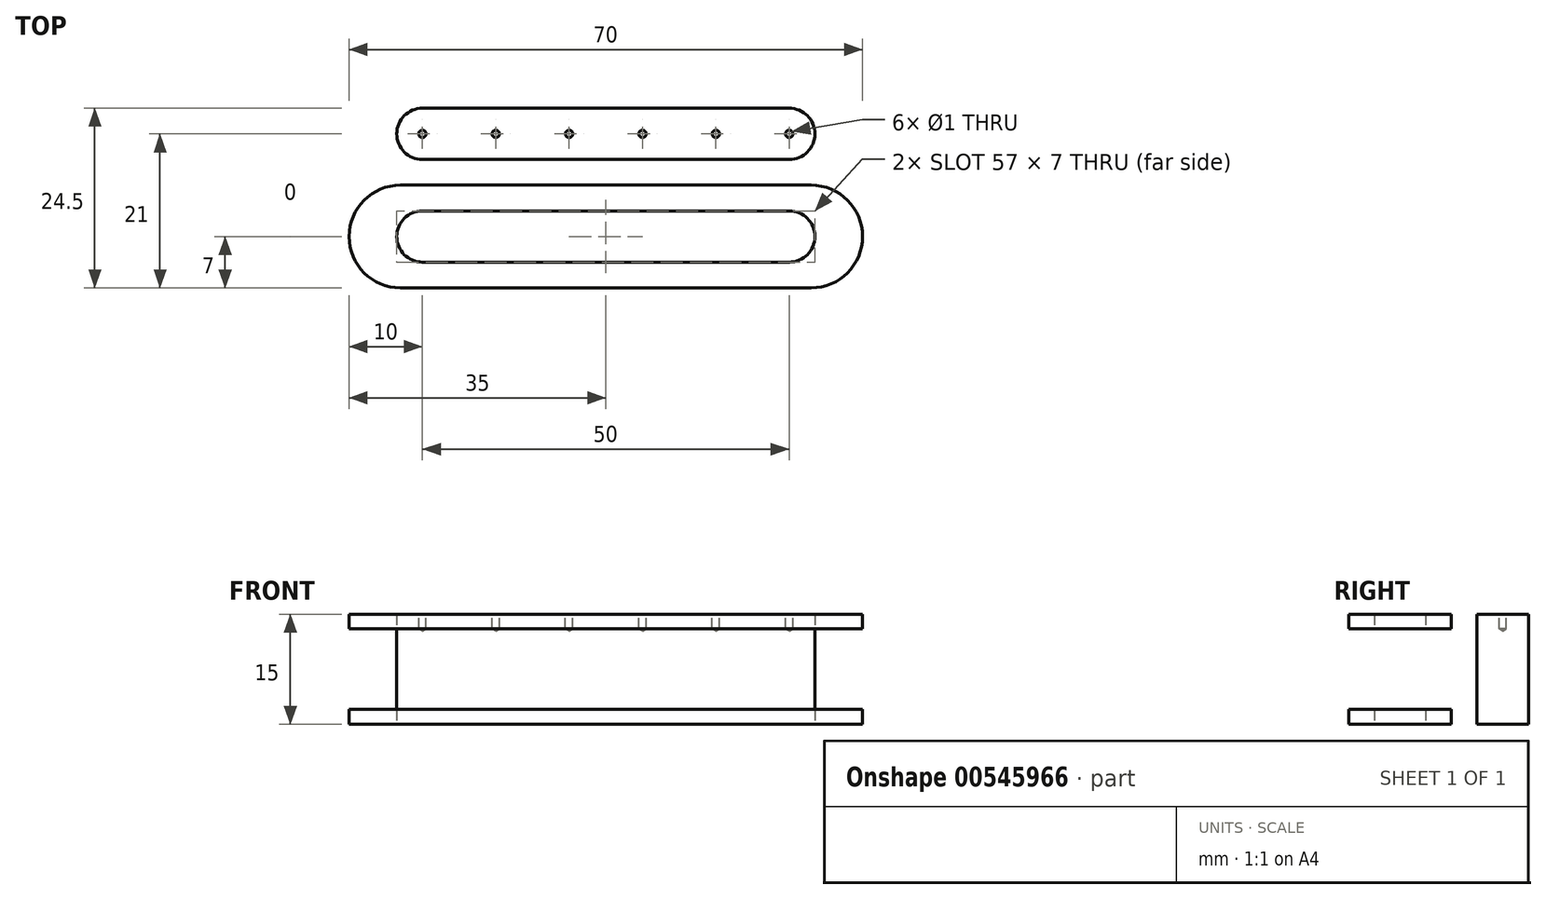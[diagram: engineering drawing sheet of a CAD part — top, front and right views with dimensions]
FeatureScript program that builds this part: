
annotation { "Feature Type Name" : "Feature", "Feature Type Description" : "" }
export const myFeature = defineFeature(function(context is Context, id is Id, definition is map)
    precondition{}
    {
        {
            var Q0;
            Q0=qCreatedBy(makeId("Top.planeOp"),FACE);
            var sketch = newSketch(context, id + "F0", { "sketchPlane" : qUnion([Q0])});
            skLineSegment(sketch, "E0.bottom", {"start": v(28, -7) * mm, "end": v(-28, -7) * mm});
            skLineSegment(sketch, "E0.top", {"start": v(28, 7) * mm, "end": v(-28, 7) * mm});
            skLineSegment(sketch, "E0.left", {"start": v(35, 0) * mm, "end": v(35, 0) * mm});
            skLineSegment(sketch, "E0.right", {"start": v(-35, 0) * mm, "end": v(-35, 0) * mm});
            skPoint(sketch, "E0.middle", {"position": v(0, 0) * mm});
            skPoint(sketch, "E1.visualSharp", {"position": v(-35, 7) * mm});
            skArc(sketch, "E1.filletArc", {"start": v(-28, 7) * mm, "mid": v(-32.95, 4.95) * mm, "end": v(-35, 0) * mm});
            skPoint(sketch, "E2.visualSharp", {"position": v(-35, -7) * mm});
            skArc(sketch, "E2.filletArc", {"start": v(-35, 0) * mm, "mid": v(-32.95, -4.95) * mm, "end": v(-28, -7) * mm});
            skPoint(sketch, "E3.visualSharp", {"position": v(35, 7) * mm});
            skArc(sketch, "E3.filletArc", {"start": v(35, 0) * mm, "mid": v(32.95, 4.95) * mm, "end": v(28, 7) * mm});
            skPoint(sketch, "E4.visualSharp", {"position": v(35, -7) * mm});
            skArc(sketch, "E4.filletArc", {"start": v(28, -7) * mm, "mid": v(32.95, -4.95) * mm, "end": v(35, 0) * mm});
            skPoint(sketch, "E5", {"position": v(15, 0) * mm});
            skPoint(sketch, "E6", {"position": v(5, 0) * mm});
            skPoint(sketch, "E7", {"position": v(-5, 0) * mm});
            skPoint(sketch, "E8", {"position": v(-15, 0) * mm});
            skPoint(sketch, "E9", {"position": v(-25, 0) * mm});
            skPoint(sketch, "E10", {"position": v(25, 0) * mm});
            skLineSegment(sketch, "E11.bottom", {"start": v(25, 3.5) * mm, "end": v(-25, 3.5) * mm});
            skLineSegment(sketch, "E11.top", {"start": v(25, -3.5) * mm, "end": v(-25, -3.5) * mm});
            skLineSegment(sketch, "E11.left", {"start": v(28.5, 0) * mm, "end": v(28.5, 0) * mm});
            skLineSegment(sketch, "E11.right", {"start": v(-28.5, 0) * mm, "end": v(-28.5, 0) * mm});
            skPoint(sketch, "E12.visualSharp", {"position": v(-28.5, 3.5) * mm});
            skArc(sketch, "E12.filletArc", {"start": v(-25, 3.5) * mm, "mid": v(-27.47, 2.47) * mm, "end": v(-28.5, 0) * mm});
            skPoint(sketch, "E13.visualSharp", {"position": v(-28.5, -3.5) * mm});
            skArc(sketch, "E13.filletArc", {"start": v(-28.5, 0) * mm, "mid": v(-27.47, -2.47) * mm, "end": v(-25, -3.5) * mm});
            skPoint(sketch, "E14.visualSharp", {"position": v(28.5, -3.5) * mm});
            skArc(sketch, "E14.filletArc", {"start": v(25, -3.5) * mm, "mid": v(27.47, -2.47) * mm, "end": v(28.5, 0) * mm});
            skPoint(sketch, "E15.visualSharp", {"position": v(28.5, 3.5) * mm});
            skArc(sketch, "E15.filletArc", {"start": v(28.5, 0) * mm, "mid": v(27.47, 2.47) * mm, "end": v(25, 3.5) * mm});
            skSolve(sketch);
        }
        {
            var Q0;
            Q0=makeQuery(id+"F0.imprint","IMPRINT",FACE,{"disambiguationData":[TD([[makeQuery(id+"F0.imprint","IMPRINT",EDGE,{"derivedFrom":sQuery(id+"F0.wireOp",EDGE,"E11.bottom")}),1.0]])]});
            extrude(context, id + "F1", {"entities" : qUnion([Q0]), "depth" : 15 * mm, "offsetDistance" : 25 * mm});
        }
        {
            var Q0;
            Q0=qSketchRegion(id+"F0",true);
            extrude(context, id + "F2", {"entities" : qUnion([Q0]), "depth" : 2 * mm, "offsetDistance" : 25 * mm});
        }
        {
            var Q0;
            Q0=makeQuery(id+"F2.opExtrude","SWEPT_BODY",BODY,{"disambiguationData":[OSD([sQuery(id+"F0.wireOp",EDGE,"E0.bottom"),sQuery(id+"F0.wireOp",EDGE,"E0.top"),sQuery(id+"F0.wireOp",EDGE,"E1.filletArc"),sQuery(id+"F0.wireOp",EDGE,"E2.filletArc"),sQuery(id+"F0.wireOp",EDGE,"E3.filletArc"),sQuery(id+"F0.wireOp",EDGE,"E4.filletArc"),sQuery(id+"F0.wireOp",EDGE,"E11.bottom"),sQuery(id+"F0.wireOp",EDGE,"E11.top"),sQuery(id+"F0.wireOp",EDGE,"E12.filletArc"),sQuery(id+"F0.wireOp",EDGE,"E13.filletArc"),sQuery(id+"F0.wireOp",EDGE,"E14.filletArc"),sQuery(id+"F0.wireOp",EDGE,"E15.filletArc")])]});
            var Q1;
            Q1=makeQuery(id+"F1.opExtrude","SWEPT_EDGE",EDGE,{"disambiguationData":[OSD([sQuery(id+"F0.wireOp",EDGE,"E11.bottom"),sQuery(id+"F0.wireOp",EDGE,"E12.filletArc")])]});
            transform(context, id + "F3", {"entities" : qUnion([Q0]), "transformType" : TransformType.TRANSLATION_DISTANCE, "transformDirection" : qUnion([Q1]), "distance" : 13 * mm, "oppositeDirection" : true, "makeCopy" : true});
        }
        {
            var Q0;
            Q0=sQuery(id+"F0.wireOp",VERTEX,"E9");
            var Q1;
            Q1=sQuery(id+"F0.wireOp",VERTEX,"E8");
            var Q2;
            Q2=sQuery(id+"F0.wireOp",VERTEX,"E7");
            var Q3;
            Q3=sQuery(id+"F0.wireOp",VERTEX,"E6");
            var Q4;
            Q4=sQuery(id+"F0.wireOp",VERTEX,"E5");
            var Q5;
            Q5=sQuery(id+"F0.wireOp",VERTEX,"E10");
            var Q6;
            Q6=makeQuery(id+"F1.opExtrude","SWEPT_BODY",BODY,{"disambiguationData":[OSD([sQuery(id+"F0.wireOp",EDGE,"E11.bottom"),sQuery(id+"F0.wireOp",EDGE,"E11.top"),sQuery(id+"F0.wireOp",EDGE,"E12.filletArc"),sQuery(id+"F0.wireOp",EDGE,"E13.filletArc"),sQuery(id+"F0.wireOp",EDGE,"E14.filletArc"),sQuery(id+"F0.wireOp",EDGE,"E15.filletArc")])]});
            hole(context, id + "F4", {"style" : HoleStyle.SIMPLE, "endStyle" : HoleEndStyle.BLIND, "oppositeDirection" : true, "holeDiameter" : 1 * mm, "holeDepth" : 2 * mm, "isTappedThrough" : true, "tappedDepth" : 12 * mm, "tapClearance" : 3, "startFromSketch" : true, "locations" : qUnion([Q0, Q1, Q2, Q3, Q4, Q5]), "scope" : qUnion([Q6])});
        }
        {
            var Q0;
            Q0=makeQuery(id+"F1.opExtrude","SWEPT_BODY",BODY,{"disambiguationData":[OSD([sQuery(id+"F0.wireOp",EDGE,"E11.bottom"),sQuery(id+"F0.wireOp",EDGE,"E11.top"),sQuery(id+"F0.wireOp",EDGE,"E12.filletArc"),sQuery(id+"F0.wireOp",EDGE,"E13.filletArc"),sQuery(id+"F0.wireOp",EDGE,"E14.filletArc"),sQuery(id+"F0.wireOp",EDGE,"E15.filletArc")])]});
            var Q1;
            Q1=makeQuery(id+"F2.opExtrude","CAP_EDGE",EDGE,{"disambiguationData":[OSD([sQuery(id+"F0.wireOp",EDGE,"E0.top")])],"isStart":false});
            transform(context, id + "F5", {"entities" : qUnion([Q0]), "transformType" : TransformType.ROTATION, "transformAxis" : qUnion([Q1]), "angle" : 180 * degree, "makeCopy" : false});
        }
        {
            var Q0;
            Q0=makeQuery(id+"F1.opExtrude","SWEPT_BODY",BODY,{"disambiguationData":[OSD([sQuery(id+"F0.wireOp",EDGE,"E11.bottom"),sQuery(id+"F0.wireOp",EDGE,"E11.top"),sQuery(id+"F0.wireOp",EDGE,"E12.filletArc"),sQuery(id+"F0.wireOp",EDGE,"E13.filletArc"),sQuery(id+"F0.wireOp",EDGE,"E14.filletArc"),sQuery(id+"F0.wireOp",EDGE,"E15.filletArc")])]});
            var Q1;
            Q1=makeQuery(id+"F1.opExtrude","SWEPT_EDGE",EDGE,{"disambiguationData":[OSD([sQuery(id+"F0.wireOp",EDGE,"E11.bottom"),sQuery(id+"F0.wireOp",EDGE,"E12.filletArc")])]});
            transform(context, id + "F6", {"entities" : qUnion([Q0]), "transformType" : TransformType.TRANSLATION_DISTANCE, "transformDirection" : qUnion([Q1]), "distance" : 11 * mm, "makeCopy" : false});
        }
    });
